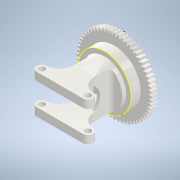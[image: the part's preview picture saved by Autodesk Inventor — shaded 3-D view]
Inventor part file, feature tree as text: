
AUTODESK INVENTOR PART (.ipt)
format: ipt  version: 2022 (Build 260153070, 153G)  size: 562,176 bytes
history: native  units: mm (DEFAULTED — no unit token found)
features: other x11, sketch x11, extrude x7, plane x5, reference x3, mirror x2, loft x1, fillet x1, projected_geometry x1
ambient origin geometry x8: Origin, YZ Plane, XZ Plane, XY Plane, X Axis, Y Axis, Z Axis, Center Point
bodies: Solid1 (feature_tree)
feature tree (42):
  extrude  "Extrusion1"  Depth=3.0mm TaperAngle=0.0deg
  plane  "Work Plane2"
  other  "Spur Gear"
  sketch  "Sketch4"  dims[d16=21.0mm d17=0.0mm]
  plane  "Work Plane11"
  extrude  "Extrusion3"  Depth=10.0mm TaperAngle=0.0deg
  plane  "Work Plane12"
  extrude  "Extrusion4"  TaperAngle=0.0deg  [1 undecoded]
  extrude  "Extrusion5"  Depth=21.0mm
  sketch  "Sketch7"  dims[d53=2.0mm d54=3.8mm d55=0.0mm]
  plane  "Work Plane13"
  other  "Work Point2"
  other  "Work Point3"
  extrude  "Extrusion6"  Depth=10.0mm TaperAngle=0.0deg
  plane  "Work Plane15"
  extrude  "Extrusion8"  Depth=2.0mm TaperAngle=0.0deg
  sketch  "Sketch13"  dims[d63=2.476182mm]
  loft  "Loft1"
  mirror  "Mirror2"
  extrude  "Extrusion9"  Depth=3.0mm
  mirror  "Mirror3"
  fillet  "Fillet1"  Radius=3.0mm
  sketch  "Sketch15"  dims[d65=2.5mm d66=1.0mm d67=1.0mm d69=4.0mm d70=0.0mm d71=22.74mm d73=10.0mm d74=10.0mm d75=6.372812mm d81=2.0mm d82=0.0mm d83=0.0mm d84=90.0deg d85=0.0mm d86=90.0deg d87=12.0mm d88=1.5mm d89=0.0mm d90=2.0mm]
  sketch  "Sketch1"  dims[d0=37.2mm d1=3.0mm d2=0.0mm]
  sketch  "Sketch2"  dims[d3=36.0mm d4=10.0mm d5=0.0mm]
  other  "Srf1"
  reference  "Reference3"
  reference  "Reference4"
  sketch  "Sketch5"  dims[d41=0.0mm d43=21.0mm]
  sketch  "Sketch6"  dims[d46=21.0mm d51=10.0mm d52=0.0mm]
  projected_geometry  "Projected Loop1"
  other  "Work Point1"
  sketch  "Sketch10"  dims[d56=1.0mm d57=0.0mm d58=1.5mm]
  sketch  "Sketch12"  dims[d59=22.0mm d61=3.0mm d62=3.0mm]
  other  "Edges1"
  reference  "Reference8"
  sketch  "Sketch14"  dims[d64=2.5mm]
  other  "Pitch Diameter"
  other  "<userpath> laptop\Desktop\SumoBot\sumobotLIDAR\sumobotLIDAR.iam"
  other  "sumobotLIDAR.iam"
  other  "608ZZ bearing:1"
  other  "Adapterlowerplate:1"
note: 1 required parameter value undecoded (feature->parameter linkage not recoverable at this tier; creation-order binding heuristic only, values carry confidence <= 0.55)
